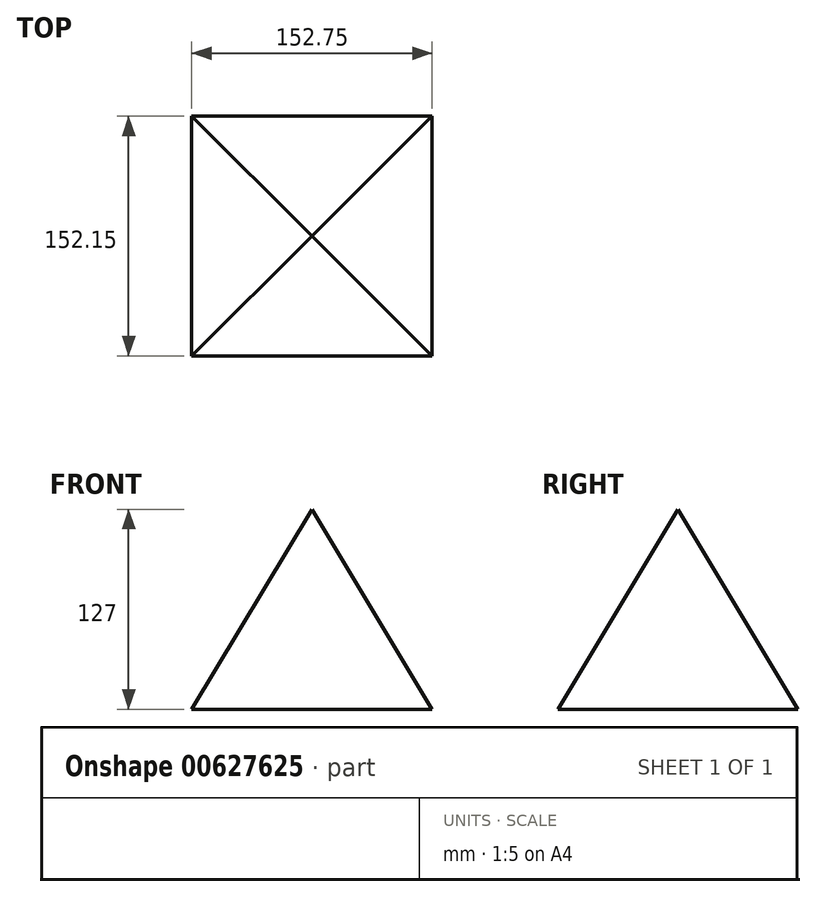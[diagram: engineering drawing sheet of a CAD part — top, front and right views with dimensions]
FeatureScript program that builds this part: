
annotation { "Feature Type Name" : "Feature", "Feature Type Description" : "" }
export const myFeature = defineFeature(function(context is Context, id is Id, definition is map)
    precondition{}
    {
        {
            var Q0;
            Q0=qCreatedBy(makeId("Top.planeOp"),FACE);
            var sketch = newSketch(context, id + "F0", { "sketchPlane" : qUnion([Q0])});
            skLineSegment(sketch, "E0.bottom", {"start": v(-76.55, 75.95) * mm, "end": v(76.2, 75.95) * mm});
            skLineSegment(sketch, "E0.top", {"start": v(-76.55, -76.2) * mm, "end": v(76.2, -76.2) * mm});
            skLineSegment(sketch, "E0.left", {"start": v(-76.55, 75.95) * mm, "end": v(-76.55, -76.2) * mm});
            skLineSegment(sketch, "E0.right", {"start": v(76.2, 75.95) * mm, "end": v(76.2, -76.2) * mm});
            skSolve(sketch);
        }
        {
            var Q0;
            Q0=makeQuery(id+"F0.imprint","IMPRINT",FACE,{"disambiguationData":[TD([[makeQuery(id+"F0.imprint","IMPRINT",EDGE,{"derivedFrom":sQuery(id+"F0.wireOp",EDGE,"E0.bottom")}),-1.0]])]});
            cPlane(context, id + "F1", {"entities" : qUnion([Q0]), "cplaneType" : CPlaneType.OFFSET, "offset" : 127 * mm, "width" : 152.4 * mm, "height" : 152.4 * mm});
        }
        {
            var Q0;
            Q0=qCreatedBy(id+"F1.planeOp",FACE);
            var sketch = newSketch(context, id + "F2", { "sketchPlane" : qUnion([Q0])});
            skCircle(sketch, "E1", {"center": v(0, 0) * mm, "radius": 0.04 * mm});
            skSolve(sketch);
        }
        {
            var Q0;
            Q0=makeQuery(id+"F0.imprint","IMPRINT",FACE,{"disambiguationData":[TD([[makeQuery(id+"F0.imprint","IMPRINT",EDGE,{"derivedFrom":sQuery(id+"F0.wireOp",EDGE,"E0.bottom")}),-1.0]])]});
            var Q1;
            Q1=sQuery(id+"F2.wireOp",VERTEX,"E1.center");
            loft(context, id + "F3", {"sheetProfilesArray" : [{ "sheetProfileEntities" : qUnion([Q0]) }, { "sheetProfileEntities" : qUnion([Q1]) }]});
        }
    });
